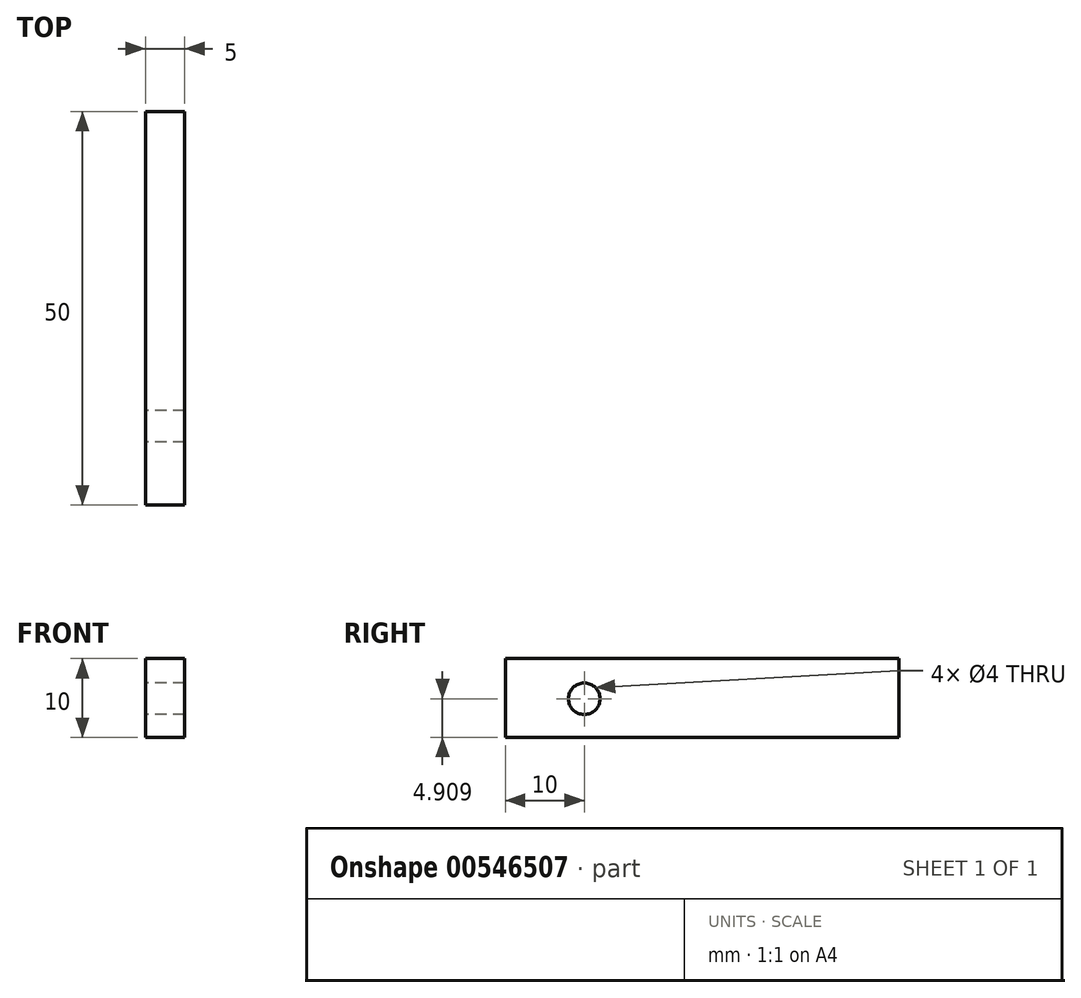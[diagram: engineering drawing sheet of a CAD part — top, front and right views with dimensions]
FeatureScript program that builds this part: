
annotation { "Feature Type Name" : "Feature", "Feature Type Description" : "" }
export const myFeature = defineFeature(function(context is Context, id is Id, definition is map)
    precondition{}
    {
        {
            var Q0;
            Q0=qCreatedBy(makeId("Right.planeOp"),FACE);
            var sketch = newSketch(context, id + "F0", { "sketchPlane" : qUnion([Q0])});
            skLineSegment(sketch, "E0", {"start": v(-20, 0) * mm, "end": v(-20, 10) * mm});
            skLineSegment(sketch, "E1", {"start": v(-20, 10) * mm, "end": v(30, 10) * mm});
            skCircle(sketch, "E2", {"center": v(-10, 4.9) * mm, "radius": 2 * mm});
            skLineSegment(sketch, "E3", {"start": v(-20, 0) * mm, "end": v(30, 0) * mm});
            skLineSegment(sketch, "E4", {"start": v(30, 0) * mm, "end": v(30, 10) * mm});
            skSolve(sketch);
        }
        {
            var Q0;
            Q0=makeQuery(id+"F0.imprint","IMPRINT",FACE,{"disambiguationData":[TD([[makeQuery(id+"F0.imprint","IMPRINT",EDGE,{"derivedFrom":sQuery(id+"F0.wireOp",EDGE,"E0")}),-1.0]])]});
            var Q1;
            Q1=sQuery(id+"F0.wireOp",EDGE,"E0");
            extrude(context, id + "F1", {"entities" : qUnion([Q0]), "surfaceEntities" : qUnion([Q1]), "depth" : 5 * mm, "offsetDistance" : 25 * mm});
        }
    });
